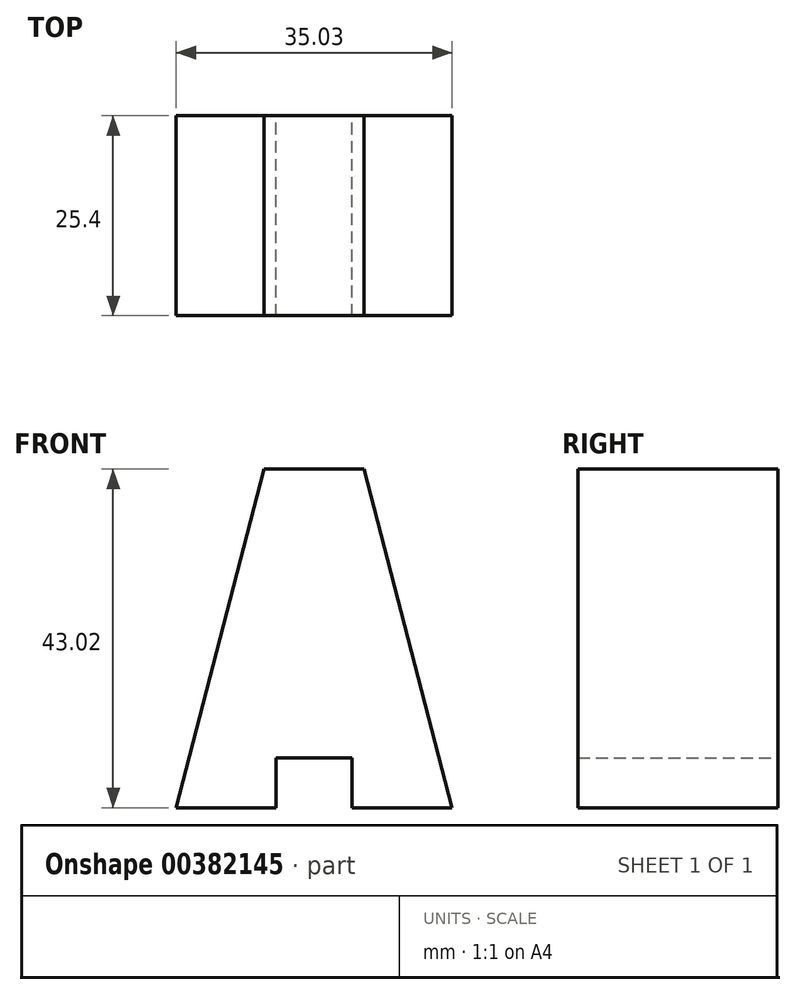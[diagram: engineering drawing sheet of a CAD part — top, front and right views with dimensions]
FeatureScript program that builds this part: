
annotation { "Feature Type Name" : "Feature", "Feature Type Description" : "" }
export const myFeature = defineFeature(function(context is Context, id is Id, definition is map)
    precondition{}
    {
        {
            var Q0;
            Q0=qCreatedBy(makeId("Front.planeOp"),FACE);
            var sketch = newSketch(context, id + "F0", { "sketchPlane" : qUnion([Q0])});
            skLineSegment(sketch, "E0", {"start": v(0, 0) * mm, "end": v(11.17, 43.02) * mm});
            skLineSegment(sketch, "E1", {"start": v(11.17, 43.02) * mm, "end": v(23.87, 43.02) * mm});
            skLineSegment(sketch, "E2", {"start": v(23.87, 43.02) * mm, "end": v(35.03, 0) * mm});
            skLineSegment(sketch, "E3", {"start": v(35.03, 0) * mm, "end": v(22.33, 0) * mm});
            skLineSegment(sketch, "E4", {"start": v(22.33, 0) * mm, "end": v(22.33, 6.35) * mm});
            skLineSegment(sketch, "E5", {"start": v(22.33, 6.35) * mm, "end": v(12.7, 6.35) * mm});
            skLineSegment(sketch, "E6", {"start": v(12.7, 6.35) * mm, "end": v(12.7, 0) * mm});
            skLineSegment(sketch, "E7", {"start": v(12.7, 0) * mm, "end": v(0, 0) * mm});
            skSolve(sketch);
        }
        {
            var Q0;
            Q0=makeQuery(id+"F0.imprint","IMPRINT",FACE,{"disambiguationData":[TD([[makeQuery(id+"F0.imprint","IMPRINT",EDGE,{"derivedFrom":sQuery(id+"F0.wireOp",EDGE,"E0")}),-1.0]])]});
            extrude(context, id + "F1", {"entities" : qUnion([Q0]), "depth" : 25.4 * mm});
        }
    });
